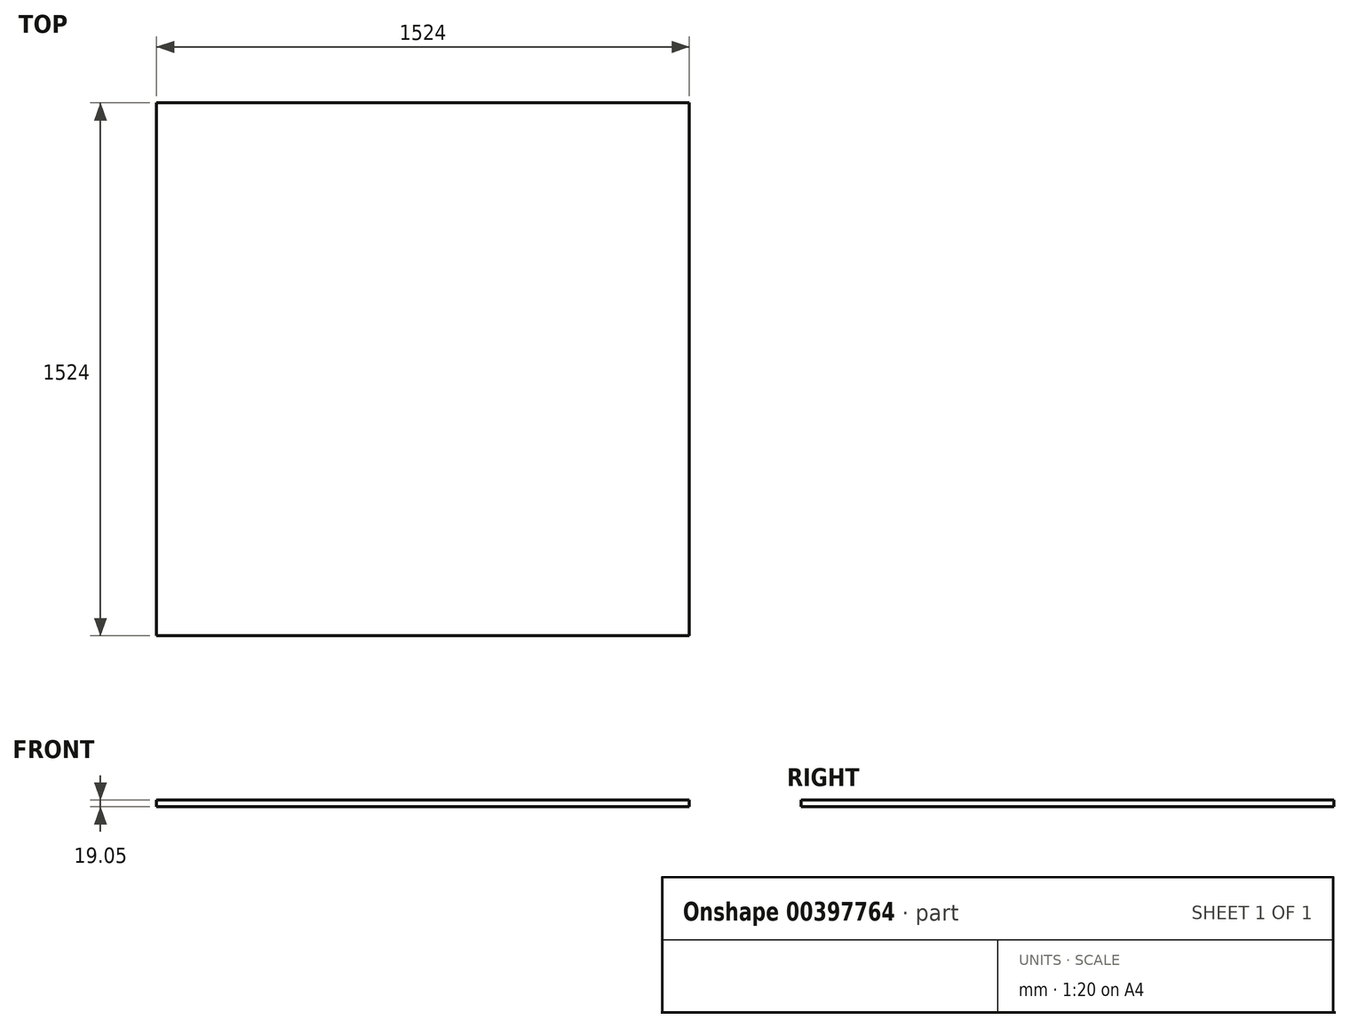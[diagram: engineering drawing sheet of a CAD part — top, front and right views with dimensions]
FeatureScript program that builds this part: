
annotation { "Feature Type Name" : "Feature", "Feature Type Description" : "" }
export const myFeature = defineFeature(function(context is Context, id is Id, definition is map)
    precondition{}
    {
        {
            var Q0;
            Q0=qCreatedBy(makeId("Top.planeOp"),FACE);
            var sketch = newSketch(context, id + "F0", { "sketchPlane" : qUnion([Q0])});
            skLineSegment(sketch, "E0.bottom", {"start": v(762, 762) * mm, "end": v(-762, 762) * mm});
            skLineSegment(sketch, "E0.top", {"start": v(762, -762) * mm, "end": v(-762, -762) * mm});
            skLineSegment(sketch, "E0.left", {"start": v(762, 762) * mm, "end": v(762, -762) * mm});
            skLineSegment(sketch, "E0.right", {"start": v(-762, 762) * mm, "end": v(-762, -762) * mm});
            skPoint(sketch, "E0.middle", {"position": v(0, 0) * mm});
            skSolve(sketch);
        }
        {
            var Q0;
            Q0 = qSketchRegion(id + "F0", true);
            extrude(context, id + "F1", {"entities" : qUnion([Q0]), "depth" : 19.05 * mm});
        }
    });
